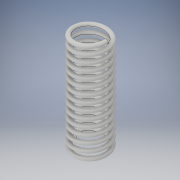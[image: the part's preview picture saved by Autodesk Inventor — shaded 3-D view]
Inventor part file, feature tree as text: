
AUTODESK INVENTOR PART (.ipt)
format: ipt  version: 2018 (Build 220112000, 112)  size: 976,384 bytes
history: native  units: in
note: dims shown in document units (in); Inventor stores cm internally (conversion verified against a paired STEP export)
features: helix x1, sketch x1
ambient origin geometry x8: Origin, YZ Plane, XZ Plane, XY Plane, X Axis, Y Axis, Z Axis, Center Point
bodies: Solid1 (feature_tree)
feature tree (2):
  helix  "Coil1"  [1 undecoded]
  sketch  "Sketch1"  dims[d1=0.09in d2=1.0in d3=0.4983in d4=5.5118in d5=0.0in d6=90.0deg d7=90.0deg d8=0.0in d9=0.0in]
note: 1 required parameter value undecoded (feature->parameter linkage not recoverable at this tier; creation-order binding heuristic only, values carry confidence <= 0.55)
